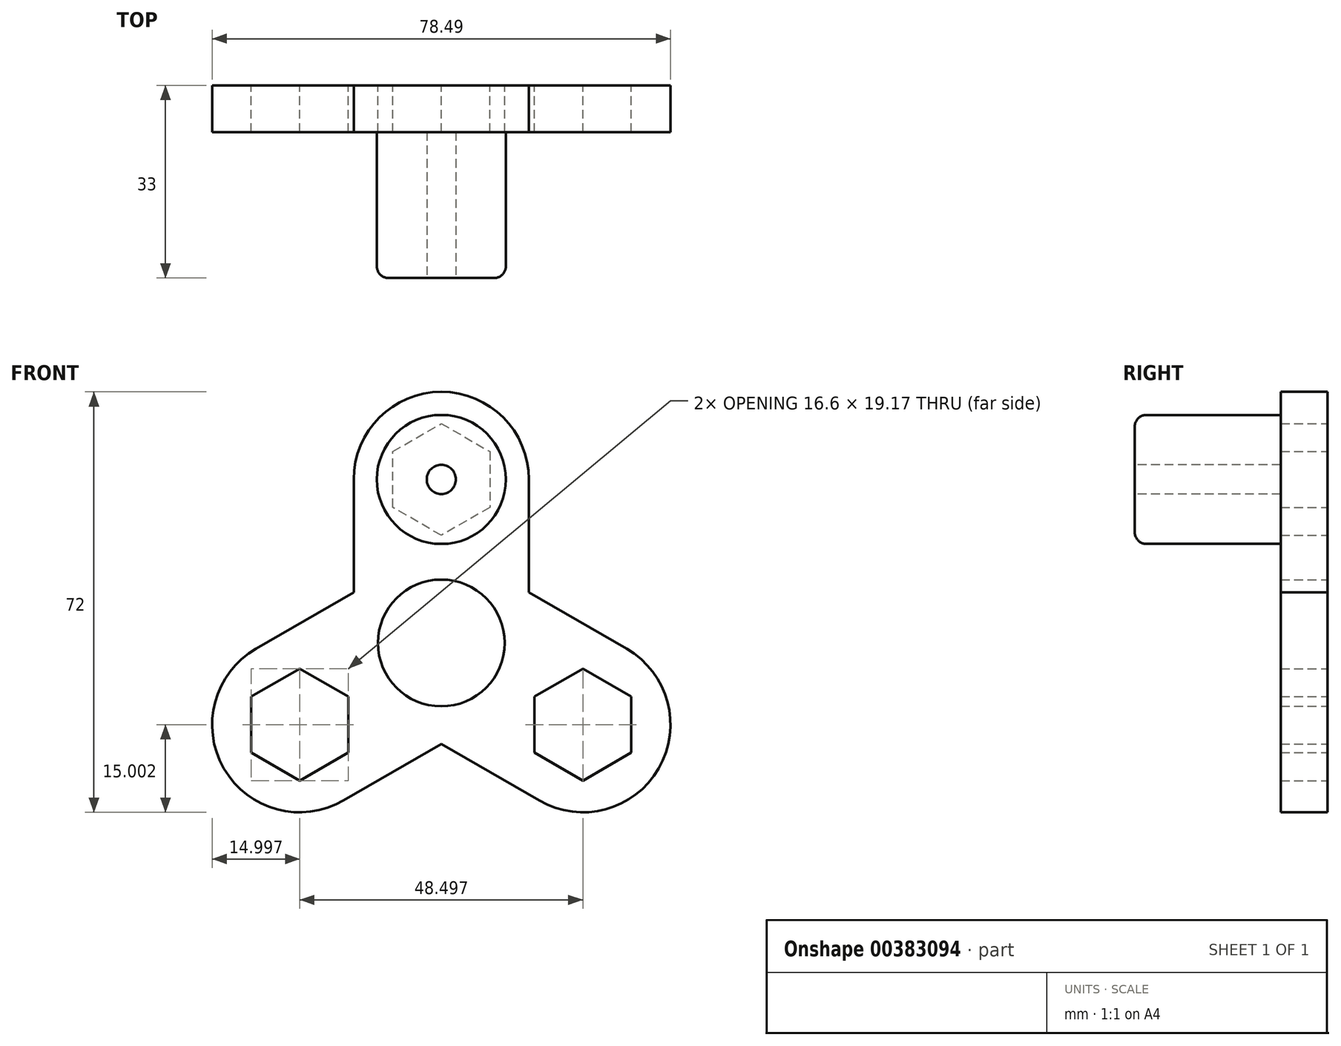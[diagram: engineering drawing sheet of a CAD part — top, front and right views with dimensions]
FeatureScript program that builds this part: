
annotation { "Feature Type Name" : "Feature", "Feature Type Description" : "" }
export const myFeature = defineFeature(function(context is Context, id is Id, definition is map)
    precondition{}
    {
        {
            var Q0;
            Q0=qCreatedBy(makeId("Front.planeOp"),FACE);
            var sketch = newSketch(context, id + "F0", { "sketchPlane" : qUnion([Q0])});
            skCircle(sketch, "E0.cCircle", {"center": v(-55.45, 69.74) * mm, "radius": 8.3 * mm, "construction": true});
            skLineSegment(sketch, "E0.0", {"start": v(-47.15, 74.53) * mm, "end": v(-47.15, 64.95) * mm});
            skLineSegment(sketch, "E0.1", {"start": v(-47.15, 64.95) * mm, "end": v(-55.45, 60.16) * mm});
            skLineSegment(sketch, "E0.2", {"start": v(-55.45, 60.16) * mm, "end": v(-63.75, 64.95) * mm});
            skLineSegment(sketch, "E0.3", {"start": v(-63.75, 64.95) * mm, "end": v(-63.75, 74.53) * mm});
            skLineSegment(sketch, "E0.4", {"start": v(-63.75, 74.53) * mm, "end": v(-55.45, 79.33) * mm});
            skLineSegment(sketch, "E0.5", {"start": v(-55.45, 79.33) * mm, "end": v(-47.15, 74.53) * mm});
            skPoint(sketch, "E0.0.midPoint", {"position": v(-47.15, 69.74) * mm});
            skArc(sketch, "E1", {"start": v(-40.45, 69.74) * mm, "mid": v(-55.45, 84.74) * mm, "end": v(-70.45, 69.74) * mm});
            skCircle(sketch, "E2", {"center": v(-55.45, 41.74) * mm, "radius": 10.85 * mm});
            skLineSegment(sketch, "E3", {"start": v(-70.45, 69.74) * mm, "end": v(-70.45, 50.4) * mm});
            skLineSegment(sketch, "E4", {"start": v(-40.45, 69.74) * mm, "end": v(-40.45, 50.4) * mm});
            skPoint(sketch, "E5.1.0", {"position": v(-83.85, 34.93) * mm});
            skLineSegment(sketch, "E5.1.2", {"start": v(-71.4, 22.95) * mm, "end": v(-79.7, 18.16) * mm});
            skLineSegment(sketch, "E5.1.3", {"start": v(-72.2, 14.75) * mm, "end": v(-55.45, 24.42) * mm});
            skArc(sketch, "E5.1.4", {"start": v(-87.2, 40.73) * mm, "mid": v(-92.7, 20.24) * mm, "end": v(-72.2, 14.75) * mm});
            skLineSegment(sketch, "E5.1.5", {"start": v(-79.7, 37.33) * mm, "end": v(-71.4, 32.53) * mm});
            skLineSegment(sketch, "E5.1.6", {"start": v(-87.2, 40.73) * mm, "end": v(-70.45, 50.4) * mm});
            skCircle(sketch, "E5.1.7", {"center": v(-79.7, 27.74) * mm, "radius": 8.3 * mm, "construction": true});
            skLineSegment(sketch, "E5.1.8", {"start": v(-88, 32.53) * mm, "end": v(-79.7, 37.33) * mm});
            skLineSegment(sketch, "E5.1.9", {"start": v(-71.4, 32.53) * mm, "end": v(-71.4, 22.95) * mm});
            skLineSegment(sketch, "E5.1.10", {"start": v(-88, 22.95) * mm, "end": v(-88, 32.53) * mm});
            skLineSegment(sketch, "E5.1.11", {"start": v(-79.7, 18.16) * mm, "end": v(-88, 22.95) * mm});
            skPoint(sketch, "E5.2.0", {"position": v(-35.36, 20.55) * mm});
            skLineSegment(sketch, "E5.2.2", {"start": v(-31.2, 37.33) * mm, "end": v(-22.9, 32.53) * mm});
            skLineSegment(sketch, "E5.2.3", {"start": v(-23.7, 40.73) * mm, "end": v(-40.45, 50.4) * mm});
            skArc(sketch, "E5.2.4", {"start": v(-38.7, 14.75) * mm, "mid": v(-18.22, 20.24) * mm, "end": v(-23.7, 40.73) * mm});
            skLineSegment(sketch, "E5.2.5", {"start": v(-39.5, 22.95) * mm, "end": v(-39.5, 32.53) * mm});
            skLineSegment(sketch, "E5.2.6", {"start": v(-38.7, 14.75) * mm, "end": v(-55.45, 24.42) * mm});
            skCircle(sketch, "E5.2.7", {"center": v(-31.2, 27.74) * mm, "radius": 8.3 * mm, "construction": true});
            skLineSegment(sketch, "E5.2.8", {"start": v(-31.2, 18.16) * mm, "end": v(-39.5, 22.95) * mm});
            skLineSegment(sketch, "E5.2.9", {"start": v(-39.5, 32.53) * mm, "end": v(-31.2, 37.33) * mm});
            skLineSegment(sketch, "E5.2.10", {"start": v(-22.9, 22.95) * mm, "end": v(-31.2, 18.16) * mm});
            skLineSegment(sketch, "E5.2.11", {"start": v(-22.9, 32.53) * mm, "end": v(-22.9, 22.95) * mm});
            skSolve(sketch);
        }
        {
            var Q0;
            Q0=makeQuery(id+"F0.imprint","IMPRINT",FACE,{"disambiguationData":[TD([[makeQuery(id+"F0.imprint","IMPRINT",EDGE,{"derivedFrom":sQuery(id+"F0.wireOp",EDGE,"E0.0")}),1.0]])]});
            extrude(context, id + "F1", {"entities" : qUnion([Q0]), "depth" : 8 * mm, "offsetDistance" : 25 * mm});
        }
        {
            var Q0;
            Q0=makeQuery(id+"F1.opExtrude","CAP_FACE",FACE,{"disambiguationData":[OSD([sQuery(id+"F0.wireOp",EDGE,"E0.0"),sQuery(id+"F0.wireOp",EDGE,"E0.1"),sQuery(id+"F0.wireOp",EDGE,"E0.2"),sQuery(id+"F0.wireOp",EDGE,"E0.3"),sQuery(id+"F0.wireOp",EDGE,"E0.4"),sQuery(id+"F0.wireOp",EDGE,"E0.5"),sQuery(id+"F0.wireOp",EDGE,"E1"),sQuery(id+"F0.wireOp",EDGE,"E2"),sQuery(id+"F0.wireOp",EDGE,"E3"),sQuery(id+"F0.wireOp",EDGE,"E4"),sQuery(id+"F0.wireOp",EDGE,"E5.1.2"),sQuery(id+"F0.wireOp",EDGE,"E5.1.3"),sQuery(id+"F0.wireOp",EDGE,"E5.1.4"),sQuery(id+"F0.wireOp",EDGE,"E5.1.5"),sQuery(id+"F0.wireOp",EDGE,"E5.1.6"),sQuery(id+"F0.wireOp",EDGE,"E5.1.8"),sQuery(id+"F0.wireOp",EDGE,"E5.1.9"),sQuery(id+"F0.wireOp",EDGE,"E5.1.10"),sQuery(id+"F0.wireOp",EDGE,"E5.1.11"),sQuery(id+"F0.wireOp",EDGE,"E5.2.2"),sQuery(id+"F0.wireOp",EDGE,"E5.2.3"),sQuery(id+"F0.wireOp",EDGE,"E5.2.4"),sQuery(id+"F0.wireOp",EDGE,"E5.2.5"),sQuery(id+"F0.wireOp",EDGE,"E5.2.6"),sQuery(id+"F0.wireOp",EDGE,"E5.2.8"),sQuery(id+"F0.wireOp",EDGE,"E5.2.9"),sQuery(id+"F0.wireOp",EDGE,"E5.2.10"),sQuery(id+"F0.wireOp",EDGE,"E5.2.11")])],"isStart":false});
            var sketch = newSketch(context, id + "F2", { "sketchPlane" : qUnion([Q0])});
            skCircle(sketch, "E6", {"center": v(-55.45, 69.74) * mm, "radius": 11.05 * mm});
            skSolve(sketch);
        }
        {
            var Q0;
            Q0 = qSketchRegion(id + "F2", true);
            extrude(context, id + "F3", {"entities" : qUnion([Q0]), "operationType" : NewBodyOperationType.ADD, "depth" : 25 * mm, "offsetDistance" : 25 * mm});
        }
        {
            var Q0;
            Q0=makeQuery(id+"F3.opExtrude","CAP_EDGE",EDGE,{"disambiguationData":[OSD([sQuery(id+"F2.wireOp",EDGE,"E6")])],"isStart":false});
            fillet(context, id + "F4", {"entities" : qUnion([Q0]), "tangentPropagation" : true, "radius" : 2 * mm, "defaultsChanged" : true, "vertexSettings" : [], "allowEdgeOverflow" : false});
        }
        {
            var Q0;
            Q0=makeQuery(id+"F3.opExtrude","CAP_FACE",FACE,{"disambiguationData":[OSD([sQuery(id+"F2.wireOp",EDGE,"E6")])],"isStart":false});
            var sketch = newSketch(context, id + "F5", { "sketchPlane" : qUnion([Q0])});
            skCircle(sketch, "E7", {"center": v(-55.45, 69.74) * mm, "radius": 2.5 * mm});
            skSolve(sketch);
        }
        {
            var Q0;
            Q0 = qSketchRegion(id + "F5", true);
            extrude(context, id + "F6", {"entities" : qUnion([Q0]), "operationType" : NewBodyOperationType.REMOVE, "oppositeDirection" : true, "depth" : 25 * mm, "offsetDistance" : 25 * mm});
        }
    });
